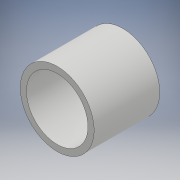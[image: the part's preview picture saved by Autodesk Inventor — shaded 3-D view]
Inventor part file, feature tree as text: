
AUTODESK INVENTOR PART (.ipt)
format: ipt  version: 2018 (Build 220112000, 112)  size: 98,816 bytes
history: native  units: mm
features: extrude x1, sketch x1
ambient origin geometry x8: Origin, YZ Plane, XZ Plane, XY Plane, X Axis, Y Axis, Z Axis, Center Point
bodies: Solid1 (feature_tree)
feature tree (2):
  extrude  "Extrusion1"  Depth=4.0mm
  sketch  "Sketch1"  dims[d0=4.5mm d1=3.75mm d2=4.0mm d3=0.0mm]
